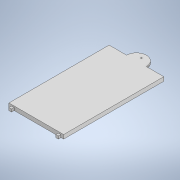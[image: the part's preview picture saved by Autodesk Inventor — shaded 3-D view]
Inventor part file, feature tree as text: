
AUTODESK INVENTOR PART (.ipt)
format: ipt  version: 2020 (Build 240168000, 168)  size: 166,912 bytes
history: native  units: mm
features: sketch x5, extrude x4, hole x1, fillet x1
ambient origin geometry x8: Origin, YZ Plane, XZ Plane, XY Plane, X Axis, Y Axis, Z Axis, Center Point
bodies: Solid1 (feature_tree)
feature tree (11):
  extrude  "Extrusion1"  Depth=76.0mm
  extrude  "Extrusion2"  Depth=2.0mm
  extrude  "Extrusion3"  Depth=2.0mm
  hole  "Hole1"  [1 undecoded]
  extrude  "Extrusion4"  Depth=2.0mm TaperAngle=0.0deg
  fillet  "Fillet1"  Radius=15.0mm
  sketch  "Sketch1"  dims[d0=41.5mm d1=76.0mm]
  sketch  "Sketch2"  dims[d2=3.0mm d3=0.0mm d4=2.0mm]
  sketch  "Sketch3"  dims[d5=2.0mm d6=2.0mm]
  sketch  "Sketch4"  dims[d7=2.0mm d8=2.0mm]
  sketch  "Sketch5"  dims[d9=2.0mm d10=2.0mm d11=0.0mm d12=15.0mm d13=1.5mm d14=0.0mm d15=3.75mm d16=1.0mm d17=6.0mm d18=4.0mm d19=2.0mm d20=90.0deg d21=2.0mm d22=20.594885mm d23=3.0mm d24=3.0mm d25=17.0mm d26=0.5mm d27=0.0mm d28=2.5mm]
note: 1 required parameter value undecoded (feature->parameter linkage not recoverable at this tier; creation-order binding heuristic only, values carry confidence <= 0.55)
